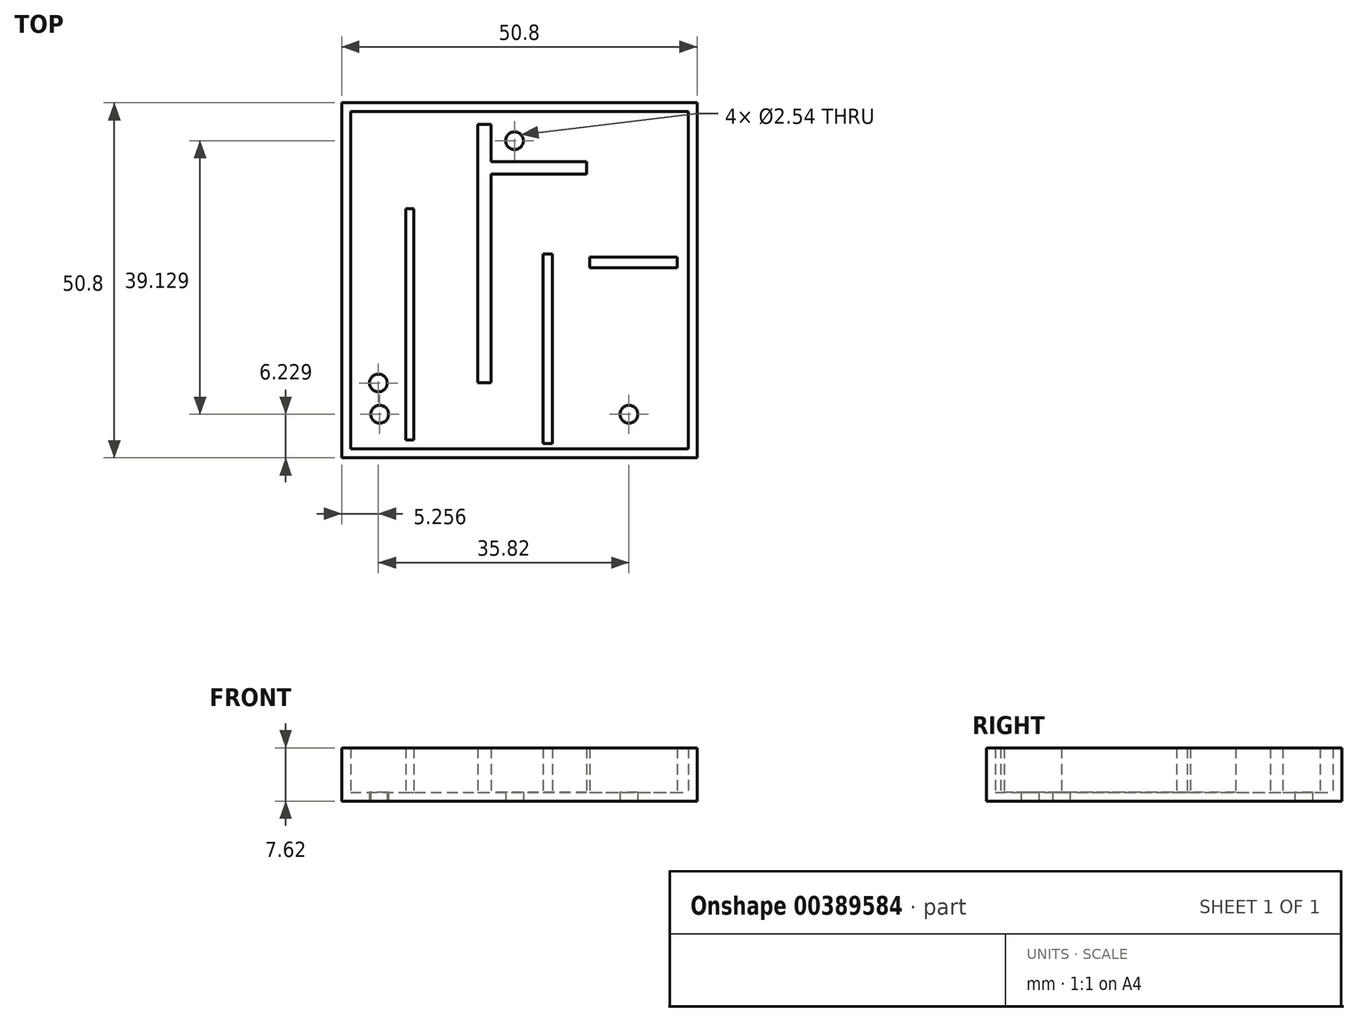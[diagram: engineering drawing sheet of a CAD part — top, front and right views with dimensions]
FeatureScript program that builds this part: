
annotation { "Feature Type Name" : "Feature", "Feature Type Description" : "" }
export const myFeature = defineFeature(function(context is Context, id is Id, definition is map)
    precondition{}
    {
        {
            var Q0;
            Q0=qCreatedBy(makeId("Top.planeOp"),FACE);
            var sketch = newSketch(context, id + "F0", { "sketchPlane" : qUnion([Q0])});
            skLineSegment(sketch, "E0.bottom", {"start": v(0, 0) * mm, "end": v(50.8, 0) * mm});
            skLineSegment(sketch, "E0.top", {"start": v(0, 50.8) * mm, "end": v(50.8, 50.8) * mm});
            skLineSegment(sketch, "E0.left", {"start": v(0, 0) * mm, "end": v(0, 50.8) * mm});
            skLineSegment(sketch, "E0.right", {"start": v(50.8, 0) * mm, "end": v(50.8, 50.8) * mm});
            skSolve(sketch);
        }
        {
            var Q0;
            Q0 = qSketchRegion(id + "F0", true);
            extrude(context, id + "F1", {"entities" : qUnion([Q0]), "depth" : 7.62 * mm});
        }
        {
            var Q0;
            Q0=makeQuery(id+"F1.opExtrude","CAP_FACE",FACE,{"disambiguationData":[OSD([sQuery(id+"F0.wireOp",EDGE,"E0.bottom"),sQuery(id+"F0.wireOp",EDGE,"E0.top"),sQuery(id+"F0.wireOp",EDGE,"E0.left"),sQuery(id+"F0.wireOp",EDGE,"E0.right")])],"isStart":false});
            shell(context, id + "F2", {"entities" : qUnion([Q0]), "thickness" : 1.27 * mm});
        }
        {
            var Q0;
            Q0=qCreatedBy(makeId("Top.planeOp"),FACE);
            var sketch = newSketch(context, id + "F3", { "sketchPlane" : qUnion([Q0])});
            skLineSegment(sketch, "E1.bottom", {"start": v(10.34, 2.54) * mm, "end": v(9.18, 2.54) * mm});
            skLineSegment(sketch, "E1.top", {"start": v(10.34, 35.66) * mm, "end": v(9.18, 35.66) * mm});
            skLineSegment(sketch, "E1.left", {"start": v(10.34, 2.54) * mm, "end": v(10.34, 35.66) * mm});
            skLineSegment(sketch, "E1.right", {"start": v(9.18, 2.54) * mm, "end": v(9.18, 35.66) * mm});
            skLineSegment(sketch, "E2.bottom", {"start": v(21.37, 47.67) * mm, "end": v(19.47, 47.67) * mm});
            skLineSegment(sketch, "E2.top", {"start": v(21.37, 10.72) * mm, "end": v(19.47, 10.72) * mm});
            skLineSegment(sketch, "E2.left", {"start": v(21.37, 47.67) * mm, "end": v(21.37, 10.72) * mm});
            skLineSegment(sketch, "E2.right", {"start": v(19.47, 47.67) * mm, "end": v(19.47, 10.72) * mm});
            skLineSegment(sketch, "E3.bottom", {"start": v(30.12, 2.04) * mm, "end": v(28.76, 2.04) * mm});
            skLineSegment(sketch, "E3.top", {"start": v(30.12, 29.14) * mm, "end": v(28.76, 29.14) * mm});
            skLineSegment(sketch, "E3.left", {"start": v(30.12, 2.04) * mm, "end": v(30.12, 29.14) * mm});
            skLineSegment(sketch, "E3.right", {"start": v(28.76, 2.04) * mm, "end": v(28.76, 29.14) * mm});
            skLineSegment(sketch, "E4.bottom", {"start": v(21.37, 42.34) * mm, "end": v(35.04, 42.34) * mm});
            skLineSegment(sketch, "E4.top", {"start": v(21.37, 40.61) * mm, "end": v(35.04, 40.61) * mm});
            skLineSegment(sketch, "E4.left", {"start": v(21.37, 42.34) * mm, "end": v(21.37, 40.61) * mm});
            skLineSegment(sketch, "E4.right", {"start": v(35.04, 42.34) * mm, "end": v(35.04, 40.61) * mm});
            skLineSegment(sketch, "E5.bottom", {"start": v(48, 28.69) * mm, "end": v(35.43, 28.69) * mm});
            skLineSegment(sketch, "E5.top", {"start": v(48, 27.17) * mm, "end": v(35.43, 27.17) * mm});
            skLineSegment(sketch, "E5.left", {"start": v(48, 28.69) * mm, "end": v(48, 27.17) * mm});
            skLineSegment(sketch, "E5.right", {"start": v(35.43, 28.69) * mm, "end": v(35.43, 27.17) * mm});
            skSolve(sketch);
        }
        {
            var Q0;
            Q0 = qSketchRegion(id + "F3", true);
            extrude(context, id + "F4", {"entities" : qUnion([Q0]), "operationType" : NewBodyOperationType.ADD, "depth" : 7.62 * mm});
        }
        {
            var Q0;
            Q0=qCreatedBy(makeId("Top.planeOp"),FACE);
            var sketch = newSketch(context, id + "F5", { "sketchPlane" : qUnion([Q0])});
            skCircle(sketch, "E6", {"center": v(5.45, 6.23) * mm, "radius": 1.27 * mm});
            skCircle(sketch, "E7", {"center": v(5.26, 10.7) * mm, "radius": 1.27 * mm});
            skCircle(sketch, "E8", {"center": v(41.08, 6.23) * mm, "radius": 1.27 * mm});
            skCircle(sketch, "E9", {"center": v(24.72, 45.36) * mm, "radius": 1.27 * mm});
            skSolve(sketch);
        }
        {
            var Q0;
            Q0 = qSketchRegion(id + "F5", true);
            extrude(context, id + "F6", {"entities" : qUnion([Q0]), "operationType" : NewBodyOperationType.REMOVE, "endBound" : BoundingType.THROUGH_ALL, "depth" : 25.4 * mm});
        }
    });
